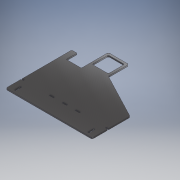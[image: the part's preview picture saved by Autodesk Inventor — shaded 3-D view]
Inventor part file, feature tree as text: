
AUTODESK INVENTOR PART (.ipt)
format: ipt  version: 2018 (Build 220112000, 112)  size: 247,296 bytes
history: native  units: mm
features: extrude x4, sketch x4, fillet x3, other x1
ambient origin geometry x8: Origin, YZ Plane, XZ Plane, XY Plane, X Axis, Y Axis, Z Axis, Center Point
bodies: Body1 (feature_tree)
feature tree (12):
  other  "Sólido1"
  extrude  "Extrusión1"  Depth=20.0mm
  fillet  "Empalme1"  Radius=25.0mm
  fillet  "Empalme2"  Radius=50.0mm
  extrude  "Extrusión2"  Depth=2.0mm
  extrude  "Extrusión3"  Depth=6.0mm TaperAngle=0.0deg
  extrude  "Extrusión4"  Depth=70.0mm
  fillet  "Empalme3"  Radius=10.0mm
  sketch  "Boceto1"  dims[d0=305.0mm d1=95.0mm d2=95.0mm d3=195.0mm d4=400.0mm d7=75.0mm d8=75.0mm d9=20.0mm d10=25.0mm d11=50.0mm]
  sketch  "Boceto2"  dims[d12=6.0mm d13=0.0mm d14=2.0mm]
  sketch  "Boceto3"  dims[d15=6.0mm]
  sketch  "Boceto5"  dims[d16=20.0mm d17=6.0mm d18=20.0mm d19=60.0mm d20=20.0mm d21=60.0mm d22=8.0mm d23=20.0mm d24=6.0mm d25=110.0mm d27=6.0mm d28=6.0mm d29=107.0mm d31=6.0mm d32=0.0mm d33=70.0mm d34=10.0mm d35=20.0mm d36=6.0mm d38=20.0mm d39=60.0mm d40=20.0mm d41=60.0mm d42=8.0mm d43=20.0mm d44=6.0mm d45=110.0mm d46=6.0mm d47=20.0mm d48=12.0mm d49=6.0mm d50=44.0mm d51=6.0mm d52=6.0mm d54=6.0mm d55=6.0mm d56=26.0mm d57=8.0mm d58=8.0mm d59=6.0mm d60=0.0mm d61=20.0mm d62=6.0mm d63=0.0mm d64=6.0mm]
